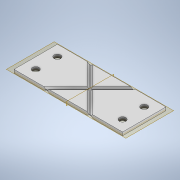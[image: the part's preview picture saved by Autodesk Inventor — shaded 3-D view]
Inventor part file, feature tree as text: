
AUTODESK INVENTOR PART (.ipt)
format: ipt  version: 2020 (Build 240168000, 168)  size: 200,704 bytes
history: native  units: mm
features: projected_geometry x6, extrude x3, sketch x3, plane x2, chamfer x1, mirror x1
ambient origin geometry x8: Origin, YZ Plane, XZ Plane, XY Plane, X Axis, Y Axis, Z Axis, Center Point
bodies: Solid1 (feature_tree)
feature tree (16):
  extrude  "Extrusion1"  Depth=20.0mm
  plane  "Work Plane1"
  extrude  "Extrusion2"  Depth=10.0mm
  chamfer  "Chamfer1"  Distance=10.0mm
  extrude  "Extrusion3"  Depth=0.675mm
  plane  "Work Plane2"
  mirror  "Mirror1"
  sketch  "Sketch1"  dims[d0=50.0mm d1=20.0mm]
  sketch  "Sketch2"  dims[d2=10.0mm d3=10.0mm]
  projected_geometry  "Projected Loop1"
  projected_geometry  "Projected Loop2"
  projected_geometry  "Projected Loop3"
  projected_geometry  "Projected Loop4"
  sketch  "Sketch3"  dims[d4=10.0mm d5=10.0mm d6=0.5mm d7=40.0mm d8=0.5mm d9=40.0mm d10=1.5mm d11=0.0mm d12=0.15mm d13=0.0mm d14=0.675mm d15=2.0mm d16=45.0deg d17=5.0mm d18=5.0mm d19=5.0mm d20=3.0mm d21=3.0mm d22=4.0mm d23=0.0mm]
  projected_geometry  "Projected Loop5"
  projected_geometry  "Projected Loop6"
